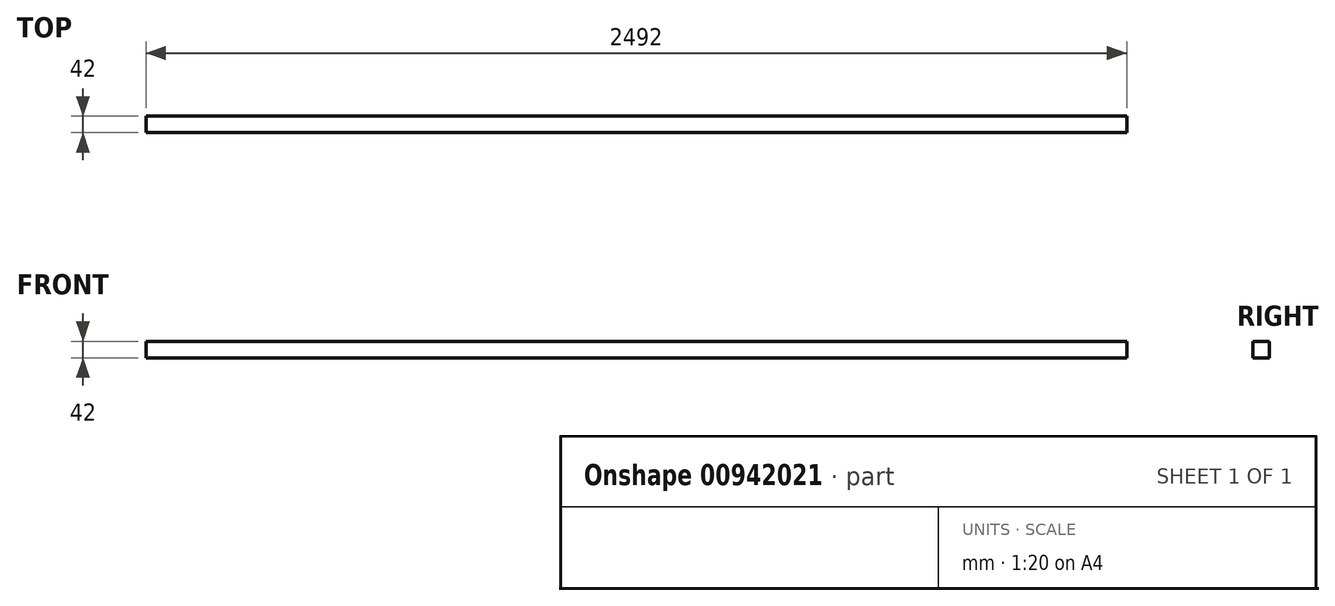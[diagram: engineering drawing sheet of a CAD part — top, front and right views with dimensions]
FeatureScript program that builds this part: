
annotation { "Feature Type Name" : "Feature", "Feature Type Description" : "" }
export const myFeature = defineFeature(function(context is Context, id is Id, definition is map)
    precondition{}
    {
        {
            var Q0;
            Q0=qCreatedBy(makeId("Right.planeOp"),FACE);
            var sketch = newSketch(context, id + "F0", { "sketchPlane" : qUnion([Q0])});
            skLineSegment(sketch, "E0.bottom", {"start": v(19.09, 7.86) * mm, "end": v(61.09, 7.86) * mm});
            skLineSegment(sketch, "E0.top", {"start": v(19.09, 49.86) * mm, "end": v(61.09, 49.86) * mm});
            skLineSegment(sketch, "E0.left", {"start": v(19.09, 7.86) * mm, "end": v(19.09, 49.86) * mm});
            skLineSegment(sketch, "E0.right", {"start": v(61.09, 7.86) * mm, "end": v(61.09, 49.86) * mm});
            skSolve(sketch);
        }
        {
            var Q0;
            Q0=makeQuery(id+"F0.imprint","IMPRINT",FACE,{"disambiguationData":[TD([[makeQuery(id+"F0.imprint","IMPRINT",EDGE,{"derivedFrom":sQuery(id+"F0.wireOp",EDGE,"E0.bottom")}),1.0]])]});
            extrude(context, id + "F1", {"entities" : qUnion([Q0]), "depth" : 2492 * mm, "offsetDistance" : 25 * mm});
        }
    });
